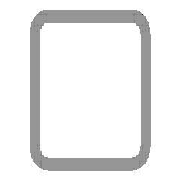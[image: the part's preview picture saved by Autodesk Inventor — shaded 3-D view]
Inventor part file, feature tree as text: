
AUTODESK INVENTOR PART (.ipt)
format: ipt  version: 2021 (Build 250183000, 183)  size: 139,776 bytes
history: native  units: mm (DEFAULTED — no unit token found)
features: other x5, sketch x3, extrude x1, split x1, plane x1
ambient origin geometry x8: Origin, YZ Plane, XZ Plane, XY Plane, X Axis, Y Axis, Z Axis, Center Point
bodies: Solid1 (feature_tree)
feature tree (11):
  parser-record x1  (decoder bookkeeping rows leaked as tree rows — omitted from the tree; the rows remain in map.json)
  other  "Driven Length"
  other  "Plano inicial"
  other  "Plano final"
  extrude  "Corpo"  TaperAngle=0.0deg  [1 undecoded]
  other  "Plano de trabalho4"
  split  "Dividir1"
  sketch  "Esboço"  dims[d11=50.8mm d12=4.7625mm d13=-0.0mm d14=2034.077676mm d15=25.4mm d16=25.4mm d17=9.525mm d18=90.0deg d19=2034.077676mm]
  sketch  "Sketch3"  dims[d3=2030.799585mm d4=0.0mm]
  plane  "Work Plane3"
  sketch  "Sketch4"  dims[d10=50.8mm]
note: 1 required parameter value undecoded (feature->parameter linkage not recoverable at this tier; creation-order binding heuristic only, values carry confidence <= 0.55)
